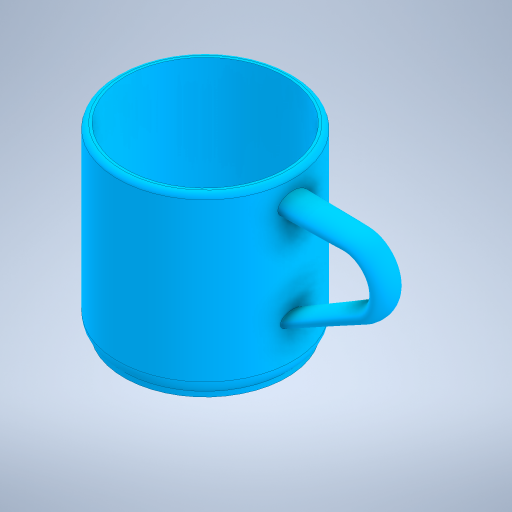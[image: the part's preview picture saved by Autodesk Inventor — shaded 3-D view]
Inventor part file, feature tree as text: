
AUTODESK INVENTOR PART (.ipt)
format: ipt  version: 2024 (Build 280153000, 153)  size: 364,032 bytes
history: native  units: in
note: dims shown in document units (in); Inventor stores cm internally (conversion verified against a paired STEP export)
features: sketch x6, other x3, plane x2, revolve x1, shell x1, loft x1, fillet x1, extrude x1
ambient origin geometry x8: Origin, YZ Plane, XZ Plane, XY Plane, X Axis, Y Axis, Z Axis, Center Point
bodies: Solid1 (feature_tree)
feature tree (16):
  other  "CrossSection1"
  revolve  "Revolution1"  [1 undecoded]
  shell  "Shell1"  Thickness=2.5591in
  sketch  "Sketch2"  dims[d4=1.2795in d5=90.0deg d6=0.1181in]
  sketch  "Sketch3"  dims[d7=0.0197in d8=0.0787in d9=0.0in d10=0.7874in d15=0.1575in]
  other  "Work Point1"
  plane  "Work Plane1"
  sketch  "Sketch4"  dims[d16=0.2362in]
  other  "Work Point2"
  plane  "Work Plane2"
  loft  "Loft1"
  fillet  "Fillet1"  Radius=0.1181in
  extrude  "Extrusion1"  Depth=0.0787in
  sketch  "Sketch1"  dims[d1=2.7559in d2=1.378in d3=2.5591in]
  sketch  "Sketch5"  dims[d17=0.1181in]
  sketch  "Sketch6"  dims[d18=0.1969in d19=0.0in d20=90.0deg d21=0.0in d22=90.0deg d23=0.0in d24=90.0deg d25=0.0787in d26=2.5591in d27=2.4409in d28=0.0787in d29=0.0in d30=0.0197in d31=0.0344in]
note: 1 required parameter value undecoded (feature->parameter linkage not recoverable at this tier; creation-order binding heuristic only, values carry confidence <= 0.55)
